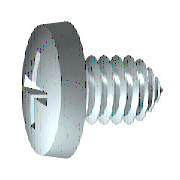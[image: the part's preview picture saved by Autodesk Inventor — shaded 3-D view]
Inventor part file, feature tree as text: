
AUTODESK INVENTOR PART (.ipt)
format: ipt  version: 2017 (Build 210142000, 142)  size: 249,856 bytes
history: native  units: mm (DEFAULTED — no unit token found)
features: other x2, plane x2, extrude x1
ambient origin geometry x8: Origin, YZ Plane, XZ Plane, XY Plane, X Axis, Y Axis, Z Axis, Center Point
bodies: Solid1 (feature_tree)
feature tree (5):
  other  "Corps"
  plane  "Work Plane1"
  extrude  "Rainure"  Depth=3.5mm
  other  "Coupe"
  plane  "Work Plane3"
